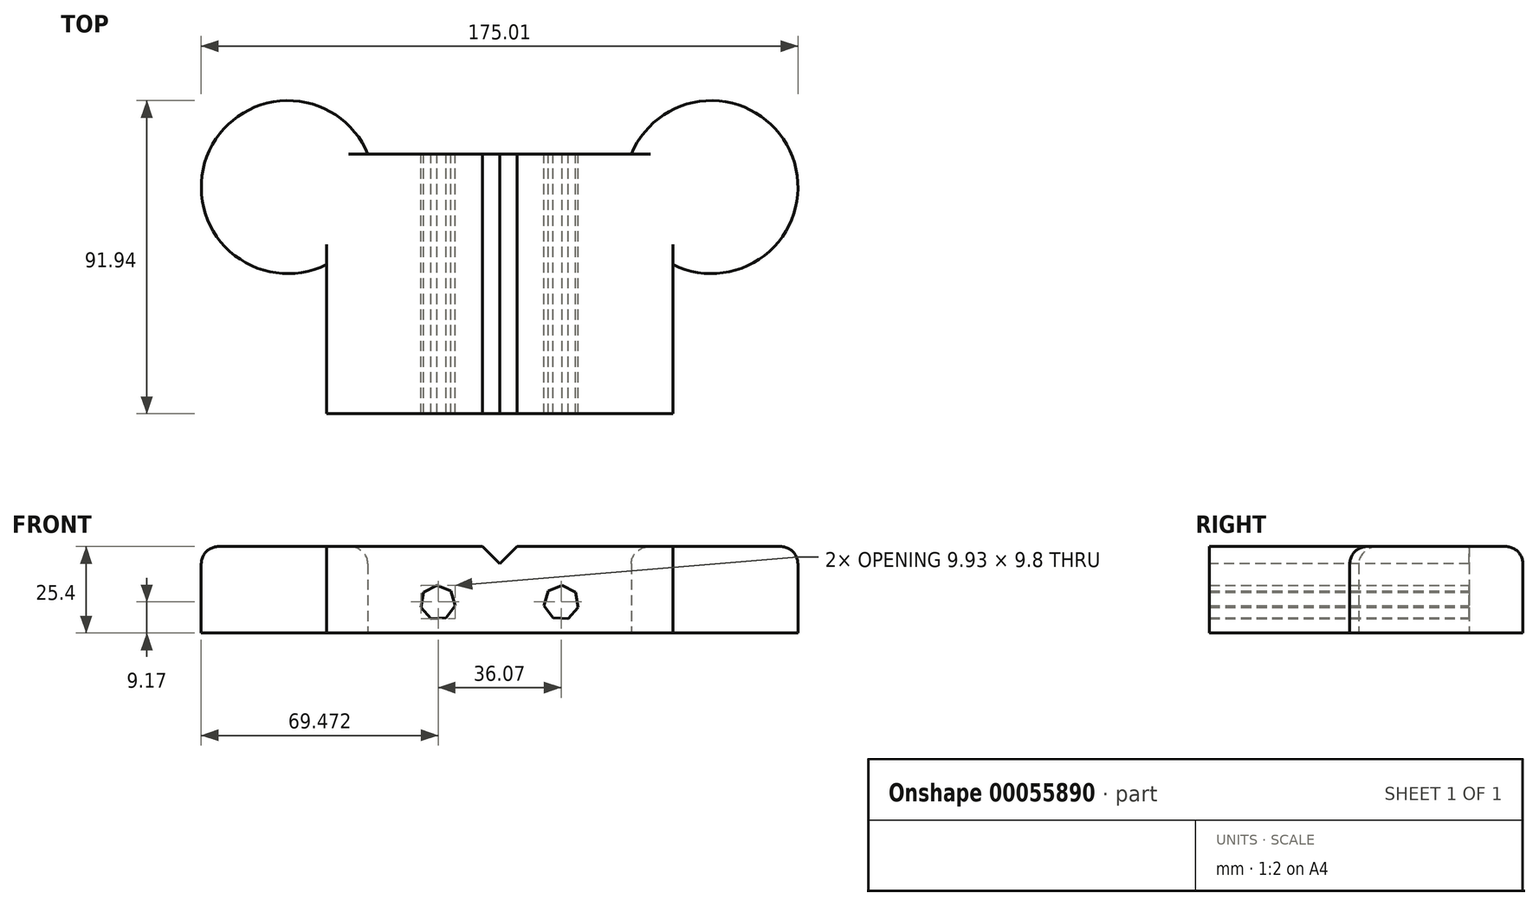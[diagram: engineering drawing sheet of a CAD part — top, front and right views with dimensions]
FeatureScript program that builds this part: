
annotation { "Feature Type Name" : "Feature", "Feature Type Description" : "" }
export const myFeature = defineFeature(function(context is Context, id is Id, definition is map)
    precondition{}
    {
        {
            var Q0;
            Q0=qCreatedBy(makeId("Top.planeOp"),FACE);
            var sketch = newSketch(context, id + "F0", { "sketchPlane" : qUnion([Q0])});
            skLineSegment(sketch, "E0.bottom", {"start": v(-29.26, -45.82) * mm, "end": v(21.54, -45.82) * mm});
            skLineSegment(sketch, "E0.top", {"start": v(-17.08, 30.38) * mm, "end": v(21.54, 30.38) * mm});
            skLineSegment(sketch, "E0.left", {"start": v(-29.26, -45.82) * mm, "end": v(-29.26, -2.03) * mm});
            skLineSegment(sketch, "E0.right", {"start": v(21.54, -45.82) * mm, "end": v(21.54, 30.38) * mm});
            skArc(sketch, "E1", {"start": v(-17.08, 30.38) * mm, "mid": v(-64.35, 29.66) * mm, "end": v(-29.26, -2.03) * mm});
            skSolve(sketch);
        }
        {
            var Q0;
            Q0=makeQuery(id+"F0.imprint","IMPRINT",FACE,{"disambiguationData":[TD([[makeQuery(id+"F0.imprint","IMPRINT",EDGE,{"derivedFrom":sQuery(id+"F0.wireOp",EDGE,"E0.bottom")}),1.0]])]});
            extrude(context, id + "F1", {"entities" : qUnion([Q0]), "depth" : 25.4 * mm});
        }
        {
            var Q0;
            Q0=makeQuery(id+"F1.opExtrude","SWEPT_FACE",FACE,{"disambiguationData":[OSD([sQuery(id+"F0.wireOp",EDGE,"E0.top")])]});
            var sketch = newSketch(context, id + "F2", { "sketchPlane" : qUnion([Q0])});
            skCircle(sketch, "E2.cCircle", {"center": v(-3.44, 8.97) * mm, "radius": 4.6 * mm, "construction": true});
            skLineSegment(sketch, "E2.0", {"start": v(1.46, 7.6) * mm, "end": v(-1.46, 4.27) * mm});
            skLineSegment(sketch, "E2.1", {"start": v(-1.46, 4.27) * mm, "end": v(-5.89, 4.5) * mm});
            skLineSegment(sketch, "E2.2", {"start": v(-5.89, 4.5) * mm, "end": v(-8.47, 8.09) * mm});
            skLineSegment(sketch, "E2.3", {"start": v(-8.47, 8.09) * mm, "end": v(-7.27, 12.35) * mm});
            skLineSegment(sketch, "E2.4", {"start": v(-7.27, 12.35) * mm, "end": v(-3.19, 14.07) * mm});
            skLineSegment(sketch, "E2.5", {"start": v(-3.19, 14.07) * mm, "end": v(0.7, 11.95) * mm});
            skLineSegment(sketch, "E2.6", {"start": v(0.7, 11.95) * mm, "end": v(1.46, 7.6) * mm});
            skPoint(sketch, "E2.0.midPoint", {"position": v(0, 5.93) * mm});
            skSolve(sketch);
        }
        {
            var Q0;
            Q0=makeQuery(id+"F2.imprint","IMPRINT",FACE,{"disambiguationData":[TD([[makeQuery(id+"F2.imprint","IMPRINT",EDGE,{"derivedFrom":sQuery(id+"F2.wireOp",EDGE,"E2.0")}),-1.0]])]});
            extrude(context, id + "F3", {"entities" : qUnion([Q0]), "operationType" : NewBodyOperationType.REMOVE, "oppositeDirection" : true, "depth" : 76.2 * mm});
        }
        {
            var Q0;
            Q0=makeQuery(id+"F1.opExtrude","CAP_EDGE",EDGE,{"disambiguationData":[OSD([sQuery(id+"F0.wireOp",EDGE,"E0.right")])],"isStart":false});
            chamfer(context, id + "F4", {"entities" : qUnion([Q0]), "width" : 5.08 * mm, "tangentPropagation" : true});
        }
        {
            var Q0;
            Q0=makeQuery(id+"F1.opExtrude","CAP_EDGE",EDGE,{"disambiguationData":[OSD([sQuery(id+"F0.wireOp",EDGE,"E1")])],"isStart":false});
            fillet(context, id + "F5", {"entities" : qUnion([Q0]), "radius" : 5.08 * mm, "tangentPropagation" : true, "allowEdgeOverflow" : false});
        }
        {
            var Q0;
            Q0=makeQuery(id+"F1.opExtrude","SWEPT_BODY",BODY,{"disambiguationData":[OSD([sQuery(id+"F0.wireOp",EDGE,"E0.bottom"),sQuery(id+"F0.wireOp",EDGE,"E0.top"),sQuery(id+"F0.wireOp",EDGE,"E0.left"),sQuery(id+"F0.wireOp",EDGE,"E0.right"),sQuery(id+"F0.wireOp",EDGE,"E1")])]});
            var Q1;
            Q1=makeQuery(id+"F1.opExtrude","SWEPT_FACE",FACE,{"disambiguationData":[OSD([sQuery(id+"F0.wireOp",EDGE,"E0.right")])]});
            mirror(context, id + "F6", {"operationType" : NewBodyOperationType.ADD, "entities" : qUnion([Q0]), "mirrorPlane" : qUnion([Q1])});
        }
    });
